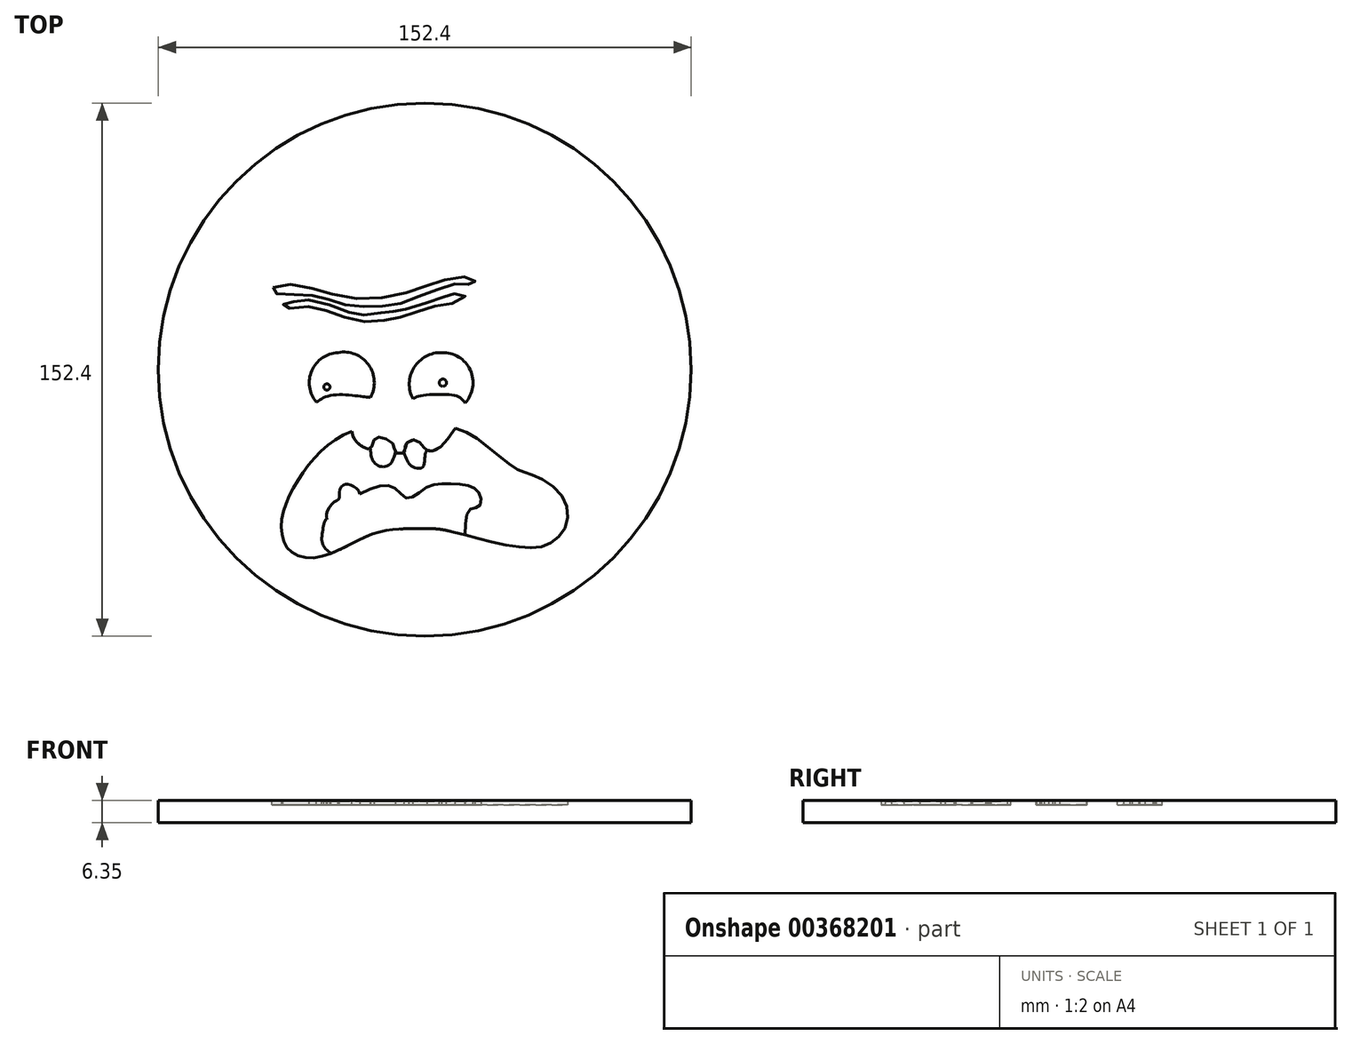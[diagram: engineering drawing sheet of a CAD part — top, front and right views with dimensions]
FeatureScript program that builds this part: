
annotation { "Feature Type Name" : "Feature", "Feature Type Description" : "" }
export const myFeature = defineFeature(function(context is Context, id is Id, definition is map)
    precondition{}
    {
        {
            var Q0;
            Q0=qCreatedBy(makeId("Top.planeOp"),FACE);
            var sketch = newSketch(context, id + "F0", { "sketchPlane" : qUnion([Q0])});
            skLineSegment(sketch, "E0", {"start": v(0, 152.4) * mm, "end": v(153.92, 0) * mm, "construction": true});
            skLineSegment(sketch, "E1", {"start": v(0, 0) * mm, "end": v(153.92, 152.4) * mm, "construction": true});
            skPoint(sketch, "E2", {"position": v(76.96, 76.2) * mm});
            skCircle(sketch, "E3", {"center": v(76.96, 76.2) * mm, "radius": 76.2 * mm});
            skSolve(sketch);
        }
        {
            var Q0;
            Q0 = qSketchRegion(id + "F0", true);
            extrude(context, id + "F1", {"entities" : qUnion([Q0]), "oppositeDirection" : true, "depth" : 6.35 * mm});
        }
        {
            var Q0;
            Q0=makeQuery(id+"F1.opExtrude","CAP_FACE",FACE,{"disambiguationData":[OSD([sQuery(id+"F0.wireOp",EDGE,"E3")])],"isStart":true});
            var sketch = newSketch(context, id + "F2", { "sketchPlane" : qUnion([Q0])});
            skLineSegment(sketch, "E4", {"start": v(0, 152.4) * mm, "end": v(153.92, 0) * mm, "construction": true});
            skLineSegment(sketch, "E5", {"start": v(0, 0) * mm, "end": v(153.92, 152.4) * mm, "construction": true});
            skPoint(sketch, "E6", {"position": v(76.96, 76.2) * mm});
            skArc(sketch, "E7", {"start": v(81.87, 81.06) * mm, "mid": v(73.9, 76.8) * mm, "end": v(73.6, 67.78) * mm});
            skArc(sketch, "E8", {"start": v(88.53, 66.66) * mm, "mid": v(89.97, 76.06) * mm, "end": v(81.87, 81.06) * mm});
            skArc(sketch, "E9", {"start": v(52.16, 81.06) * mm, "mid": v(44.65, 75.9) * mm, "end": v(45.92, 66.89) * mm});
            skCircle(sketch, "E10", {"center": v(48.96, 71.22) * mm, "radius": 0.89 * mm});
            skCircle(sketch, "E11", {"center": v(82.15, 72.45) * mm, "radius": 1.03 * mm});
            skArc(sketch, "E12", {"start": v(61.43, 68.24) * mm, "mid": v(60.86, 77.6) * mm, "end": v(52.16, 81.06) * mm});
            skFitSpline(sketch, "E13", {"points": [v(74.77, 30.7) * mm, v(62.6, 29.38) * mm, v(46.93, 22.64) * mm, v(37.99, 24.84) * mm, v(36.08, 33.34) * mm, v(40.77, 44.62) * mm, v(50.59, 55.6) * mm, v(62.9, 59.71) * mm, v(72.42, 58.4) * mm, v(84.44, 59.57) * mm, v(93.96, 54.88) * mm, v(103.34, 47.7) * mm, v(107.2, 46.27) * mm, v(115.94, 40.52) * mm, v(117.41, 31.87) * mm, v(112.43, 26.3) * mm, v(104.22, 25.42) * mm, v(90.45, 28.35) * mm, v(81.07, 30.55) * mm, v(74.77, 30.7) * mm]});
            skFitSpline(sketch, "E14", {"points": [v(56.15, 58.48) * mm, v(56.85, 56.3) * mm, v(59.27, 54.12) * mm, v(61.43, 53.63) * mm, v(62.6, 56.28) * mm, v(64.81, 56.77) * mm, v(68.2, 54.43) * mm, v(68.57, 52.52) * mm, v(70.98, 52.46) * mm, v(71.47, 54.68) * mm, v(74.36, 56.03) * mm, v(76.64, 54.12) * mm, v(77.57, 53.14) * mm, v(80.83, 53.63) * mm, v(85.2, 58.74) * mm, v(85.7, 59.39) * mm], "startDerivative": vector(6.2, -34.66) * mm, "endDerivative": vector(9.7, 11.43) * mm});
            skFitSpline(sketch, "E15", {"points": [v(50.14, 23.64) * mm, v(47.69, 26.46) * mm, v(48.04, 31.5) * mm, v(49, 33.43) * mm, v(51.09, 31.07) * mm, v(52.05, 31.95) * mm, v(54.22, 32.82) * mm, v(54.4, 36.48) * mm, v(62.24, 42.4) * mm, v(68.34, 42.31) * mm, v(72.09, 39.35) * mm, v(77.23, 42.4) * mm, v(83.15, 43.62) * mm, v(90.04, 42.84) * mm, v(92.74, 40.4) * mm, v(92.48, 37.09) * mm, v(89.86, 36.21) * mm, v(88.46, 28.89) * mm], "startDerivative": vector(-56.66, 43.32) * mm, "endDerivative": vector(-2.65, -124.19) * mm});
            skFitSpline(sketch, "E16", {"points": [v(45.92, 66.89) * mm, v(50.5, 68.88) * mm, v(59.06, 68.5) * mm, v(61.43, 68.24) * mm], "startDerivative": vector(11.59, 7.57) * mm, "endDerivative": vector(8.19, -0.86) * mm});
            skFitSpline(sketch, "E17", {"points": [v(73.6, 67.78) * mm, v(75.08, 68.57) * mm, v(81.92, 69.13) * mm, v(86.72, 68.39) * mm, v(88.53, 66.66) * mm], "startDerivative": vector(6.68, 5.13) * mm, "endDerivative": vector(7.4, -9.56) * mm});
            skFitSpline(sketch, "E18", {"points": [v(33.57, 99.73) * mm, v(40.61, 100.35) * mm, v(49.32, 98.07) * mm, v(61.43, 96.41) * mm, v(73.15, 98.7) * mm, v(80.61, 101.28) * mm, v(88.53, 102.73) * mm, v(91.39, 101.7) * mm, v(90.45, 100.14) * mm, v(88.53, 100.97) * mm, v(83.51, 99.94) * mm, v(76.57, 97.66) * mm, v(69.42, 94.86) * mm, v(62.6, 94.34) * mm, v(55.43, 94.44) * mm, v(49.63, 96.2) * mm, v(43.93, 97.45) * mm, v(37.1, 97.66) * mm, v(33.36, 98.49) * mm, v(33.57, 99.73) * mm]});
            skFitSpline(sketch, "E19", {"points": [v(39.47, 95.6) * mm, v(36.67, 95.08) * mm, v(36.57, 93.84) * mm, v(41.96, 94.15) * mm, v(49.31, 92.9) * mm, v(58.12, 90.1) * mm, v(66.4, 90.42) * mm, v(72, 91.77) * mm, v(79.47, 94.25) * mm, v(86.2, 95.6) * mm, v(88.53, 97.57) * mm, v(84.02, 97.67) * mm, v(82.47, 97.05) * mm, v(73.46, 94.05) * mm, v(68.38, 92.9) * mm, v(66.1, 92.7) * mm, v(59.88, 91.87) * mm, v(55.01, 92.7) * mm, v(44.75, 96.02) * mm, v(39.47, 95.6) * mm]});
            skPoint(sketch, "E20.orphan", {"position": v(50.8, 63.95) * mm});
            skPoint(sketch, "E21.orphan", {"position": v(83.58, 63.95) * mm});
            skSolve(sketch);
        }
        {
            var Q0;
            Q0=makeQuery(id+"F2.imprint","IMPRINT",FACE,{"disambiguationData":[TD([[makeQuery(id+"F2.imprint","IMPRINT",EDGE,{"derivedFrom":sQuery(id+"F2.wireOp",EDGE,"E19")}),1.0]])]});
            var Q1;
            Q1=makeQuery(id+"F2.imprint","IMPRINT",FACE,{"disambiguationData":[TD([[makeQuery(id+"F2.imprint","IMPRINT",EDGE,{"derivedFrom":sQuery(id+"F2.wireOp",EDGE,"E18")}),-1.0]])]});
            var Q2;
            {var subQ0=sQuery(id+"F2.wireOp",EDGE,"E14");Q2=makeQuery(id+"F2.imprint","IMPRINT",FACE,{"disambiguationData":[TD([[makeQuery(id+"F2.imprint","IMPRINT",EDGE,{"derivedFrom":subQ0}),-1.0]])]});}
            var Q3;
            Q3=makeQuery(id+"F2.imprint","IMPRINT",FACE,{"disambiguationData":[TD([[makeQuery(id+"F2.imprint","IMPRINT",EDGE,{"derivedFrom":sQuery(id+"F2.wireOp",EDGE,"E9")}),1.0]])]});
            var Q4;
            Q4=makeQuery(id+"F2.imprint","IMPRINT",FACE,{"disambiguationData":[TD([[makeQuery(id+"F2.imprint","IMPRINT",EDGE,{"derivedFrom":sQuery(id+"F2.wireOp",EDGE,"E7")}),1.0]])]});
            extrude(context, id + "F3", {"entities" : qUnion([Q0, Q1, Q2, Q3, Q4]), "operationType" : NewBodyOperationType.REMOVE, "oppositeDirection" : true, "depth" : 1.27 * mm});
        }
        {
            var Q0;
            {var subQ3=sQuery(id+"F0.wireOp",EDGE,"E3");Q0=makeQuery(id+"F3.boolean.opBoolean","SPLIT",FACE,{"disambiguationData":[TD([makeQuery(id+"F1.opExtrude","SWEPT_FACE",FACE,{"disambiguationData":[OSD([subQ3])]})])],"derivedFrom":makeQuery(id+"F1.opExtrude","CAP_FACE",FACE,{"disambiguationData":[OSD([subQ3])],"isStart":true})});}
            var sketch = newSketch(context, id + "F4", { "sketchPlane" : qUnion([Q0])});
            skLineSegment(sketch, "E22", {"start": v(0, 152.4) * mm, "end": v(153.92, 0) * mm, "construction": true});
            skLineSegment(sketch, "E23", {"start": v(0, 0) * mm, "end": v(153.92, 152.4) * mm, "construction": true});
            skPoint(sketch, "E24", {"position": v(76.96, 76.2) * mm});
            skArc(sketch, "E25", {"start": v(81.87, 81.06) * mm, "mid": v(73.9, 76.8) * mm, "end": v(73.6, 67.78) * mm});
            skArc(sketch, "E26", {"start": v(88.53, 66.66) * mm, "mid": v(89.97, 76.06) * mm, "end": v(81.87, 81.06) * mm});
            skArc(sketch, "E27", {"start": v(52.16, 81.06) * mm, "mid": v(44.65, 75.9) * mm, "end": v(45.92, 66.89) * mm});
            skCircle(sketch, "E28", {"center": v(48.96, 71.22) * mm, "radius": 0.89 * mm});
            skCircle(sketch, "E29", {"center": v(82.15, 72.45) * mm, "radius": 1.03 * mm});
            skArc(sketch, "E30", {"start": v(61.43, 68.24) * mm, "mid": v(60.86, 77.6) * mm, "end": v(52.16, 81.06) * mm});
            skFitSpline(sketch, "E31", {"points": [v(74.77, 30.7) * mm, v(62.6, 29.38) * mm, v(46.93, 22.64) * mm, v(37.99, 24.84) * mm, v(36.08, 33.34) * mm, v(40.77, 44.62) * mm, v(50.59, 55.6) * mm, v(62.9, 59.71) * mm, v(72.42, 58.4) * mm, v(84.44, 59.57) * mm, v(93.96, 54.88) * mm, v(103.34, 47.7) * mm, v(107.2, 46.27) * mm, v(115.94, 40.52) * mm, v(117.41, 31.87) * mm, v(112.43, 26.3) * mm, v(104.22, 25.42) * mm, v(90.45, 28.35) * mm, v(81.07, 30.55) * mm, v(74.77, 30.7) * mm]});
            skFitSpline(sketch, "E32", {"points": [v(56.15, 58.48) * mm, v(56.85, 56.3) * mm, v(59.27, 54.12) * mm, v(61.43, 53.63) * mm, v(62.6, 56.28) * mm, v(64.81, 56.77) * mm, v(68.2, 54.43) * mm, v(68.57, 52.52) * mm, v(70.98, 52.46) * mm, v(71.47, 54.68) * mm, v(74.36, 56.03) * mm, v(76.64, 54.12) * mm, v(77.57, 53.14) * mm, v(80.83, 53.63) * mm, v(85.2, 58.74) * mm, v(85.7, 59.39) * mm], "startDerivative": vector(6.2, -34.66) * mm, "endDerivative": vector(9.7, 11.43) * mm});
            skFitSpline(sketch, "E33", {"points": [v(50.14, 23.64) * mm, v(47.69, 26.46) * mm, v(48.04, 31.5) * mm, v(49, 33.43) * mm, v(51.09, 31.07) * mm, v(52.05, 31.95) * mm, v(54.22, 32.82) * mm, v(54.4, 36.48) * mm, v(62.24, 42.4) * mm, v(68.34, 42.31) * mm, v(72.09, 39.35) * mm, v(77.23, 42.4) * mm, v(83.15, 43.62) * mm, v(90.04, 42.84) * mm, v(92.74, 40.4) * mm, v(92.48, 37.09) * mm, v(89.86, 36.21) * mm, v(88.46, 28.89) * mm], "startDerivative": vector(-56.66, 43.32) * mm, "endDerivative": vector(-2.65, -124.19) * mm});
            skFitSpline(sketch, "E34", {"points": [v(45.92, 66.89) * mm, v(50.5, 68.88) * mm, v(59.06, 68.5) * mm, v(61.43, 68.24) * mm], "startDerivative": vector(11.59, 7.57) * mm, "endDerivative": vector(8.19, -0.86) * mm});
            skFitSpline(sketch, "E35", {"points": [v(73.6, 67.78) * mm, v(75.08, 68.57) * mm, v(81.92, 69.13) * mm, v(86.72, 68.39) * mm, v(88.53, 66.66) * mm], "startDerivative": vector(6.68, 5.13) * mm, "endDerivative": vector(7.4, -9.56) * mm});
            skFitSpline(sketch, "E36", {"points": [v(33.57, 99.73) * mm, v(40.61, 100.35) * mm, v(49.32, 98.07) * mm, v(61.43, 96.41) * mm, v(73.15, 98.7) * mm, v(80.61, 101.28) * mm, v(88.53, 102.73) * mm, v(91.39, 101.7) * mm, v(90.45, 100.14) * mm, v(88.53, 100.97) * mm, v(83.51, 99.94) * mm, v(76.57, 97.66) * mm, v(69.42, 94.86) * mm, v(62.6, 94.34) * mm, v(55.43, 94.44) * mm, v(49.63, 96.2) * mm, v(43.93, 97.45) * mm, v(37.1, 97.66) * mm, v(33.36, 98.49) * mm, v(33.57, 99.73) * mm]});
            skFitSpline(sketch, "E37", {"points": [v(39.47, 95.6) * mm, v(36.67, 95.08) * mm, v(36.57, 93.84) * mm, v(41.96, 94.15) * mm, v(49.31, 92.9) * mm, v(58.12, 90.1) * mm, v(66.4, 90.42) * mm, v(72, 91.77) * mm, v(79.47, 94.25) * mm, v(86.2, 95.6) * mm, v(88.53, 97.57) * mm, v(84.02, 97.67) * mm, v(82.47, 97.05) * mm, v(73.46, 94.05) * mm, v(68.38, 92.9) * mm, v(66.1, 92.7) * mm, v(59.88, 91.87) * mm, v(55.01, 92.7) * mm, v(44.75, 96.02) * mm, v(39.47, 95.6) * mm]});
            skPoint(sketch, "E38.orphan", {"position": v(50.8, 63.95) * mm});
            skPoint(sketch, "E39.orphan", {"position": v(83.58, 63.95) * mm});
            skSolve(sketch);
        }
        {
            var Q0;
            Q0=makeQuery(id+"F4.imprint","IMPRINT",FACE,{"disambiguationData":[TD([[makeQuery(id+"F4.imprint","IMPRINT",EDGE,{"derivedFrom":sQuery(id+"F4.wireOp",EDGE,"E33")}),-1.0]])]});
            var Q1;
            Q1=makeQuery(id+"F4.imprint","IMPRINT",FACE,{"disambiguationData":[TD([[makeQuery(id+"F4.imprint","IMPRINT",EDGE,{"derivedFrom":sQuery(id+"F4.wireOp",EDGE,"E31")}),-1.0]])]});
            extrude(context, id + "F5", {"entities" : qUnion([Q0, Q1]), "operationType" : NewBodyOperationType.REMOVE, "oppositeDirection" : true, "depth" : 0.64 * mm});
        }
        {
            var Q0;
            Q0=makeQuery(id+"F3.boolean.opBoolean","COPY",FACE,{"derivedFrom":makeQuery(id+"F3.opExtrude","CAP_FACE",FACE,{"disambiguationData":[OSD([sQuery(id+"F2.wireOp",EDGE,"E13"),sQuery(id+"F2.wireOp",EDGE,"E14"),sQuery(id+"F2.wireOp",EDGE,"E15")])],"isStart":false})});
            var sketch = newSketch(context, id + "F6", { "sketchPlane" : qUnion([Q0])});
            skLineSegment(sketch, "E40", {"start": v(0, 152.4) * mm, "end": v(153.92, 0) * mm, "construction": true});
            skLineSegment(sketch, "E41", {"start": v(0, 0) * mm, "end": v(153.92, 152.4) * mm, "construction": true});
            skPoint(sketch, "E42", {"position": v(76.96, 76.2) * mm});
            skArc(sketch, "E43", {"start": v(81.87, 81.06) * mm, "mid": v(73.9, 76.8) * mm, "end": v(73.6, 67.78) * mm});
            skArc(sketch, "E44", {"start": v(88.53, 66.66) * mm, "mid": v(89.97, 76.06) * mm, "end": v(81.87, 81.06) * mm});
            skArc(sketch, "E45", {"start": v(52.16, 81.06) * mm, "mid": v(44.65, 75.9) * mm, "end": v(45.92, 66.89) * mm});
            skCircle(sketch, "E46", {"center": v(48.96, 71.22) * mm, "radius": 0.89 * mm});
            skCircle(sketch, "E47", {"center": v(82.15, 72.45) * mm, "radius": 1.03 * mm});
            skArc(sketch, "E48", {"start": v(61.43, 68.24) * mm, "mid": v(60.86, 77.6) * mm, "end": v(52.16, 81.06) * mm});
            skFitSpline(sketch, "E49", {"points": [v(74.77, 30.7) * mm, v(62.6, 29.38) * mm, v(46.93, 22.64) * mm, v(37.99, 24.84) * mm, v(36.08, 33.34) * mm, v(40.77, 44.62) * mm, v(50.59, 55.6) * mm, v(62.9, 59.71) * mm, v(72.42, 58.4) * mm, v(84.44, 59.57) * mm, v(93.96, 54.88) * mm, v(103.34, 47.7) * mm, v(107.2, 46.27) * mm, v(115.94, 40.52) * mm, v(117.41, 31.87) * mm, v(112.43, 26.3) * mm, v(104.22, 25.42) * mm, v(90.45, 28.35) * mm, v(81.07, 30.55) * mm, v(74.77, 30.7) * mm]});
            skFitSpline(sketch, "E50", {"points": [v(56.15, 58.48) * mm, v(56.85, 56.3) * mm, v(59.27, 54.12) * mm, v(61.43, 53.63) * mm, v(62.6, 56.28) * mm, v(64.81, 56.77) * mm, v(68.2, 54.43) * mm, v(68.57, 52.52) * mm, v(70.98, 52.46) * mm, v(71.47, 54.68) * mm, v(74.36, 56.03) * mm, v(76.64, 54.12) * mm, v(77.57, 53.14) * mm, v(80.83, 53.63) * mm, v(85.2, 58.74) * mm, v(85.7, 59.39) * mm], "startDerivative": vector(6.2, -34.66) * mm, "endDerivative": vector(9.7, 11.43) * mm});
            skFitSpline(sketch, "E51", {"points": [v(50.14, 23.64) * mm, v(47.69, 26.46) * mm, v(48.04, 31.5) * mm, v(49, 33.43) * mm, v(51.09, 31.07) * mm, v(52.05, 31.95) * mm, v(54.22, 32.82) * mm, v(54.4, 36.48) * mm, v(62.24, 42.4) * mm, v(68.34, 42.31) * mm, v(72.09, 39.35) * mm, v(77.23, 42.4) * mm, v(83.15, 43.62) * mm, v(90.04, 42.84) * mm, v(92.74, 40.4) * mm, v(92.48, 37.09) * mm, v(89.86, 36.21) * mm, v(88.46, 28.89) * mm], "startDerivative": vector(-56.66, 43.32) * mm, "endDerivative": vector(-2.65, -124.19) * mm});
            skFitSpline(sketch, "E52", {"points": [v(45.92, 66.89) * mm, v(50.5, 68.88) * mm, v(59.06, 68.5) * mm, v(61.43, 68.24) * mm], "startDerivative": vector(11.59, 7.57) * mm, "endDerivative": vector(8.19, -0.86) * mm});
            skFitSpline(sketch, "E53", {"points": [v(73.6, 67.78) * mm, v(75.08, 68.57) * mm, v(81.92, 69.13) * mm, v(86.72, 68.39) * mm, v(88.53, 66.66) * mm], "startDerivative": vector(6.68, 5.13) * mm, "endDerivative": vector(7.4, -9.56) * mm});
            skFitSpline(sketch, "E54", {"points": [v(33.57, 99.73) * mm, v(40.61, 100.35) * mm, v(49.32, 98.07) * mm, v(61.43, 96.41) * mm, v(73.15, 98.7) * mm, v(80.61, 101.28) * mm, v(88.53, 102.73) * mm, v(91.39, 101.7) * mm, v(90.45, 100.14) * mm, v(88.53, 100.97) * mm, v(83.51, 99.94) * mm, v(76.57, 97.66) * mm, v(69.42, 94.86) * mm, v(62.6, 94.34) * mm, v(55.43, 94.44) * mm, v(49.63, 96.2) * mm, v(43.93, 97.45) * mm, v(37.1, 97.66) * mm, v(33.36, 98.49) * mm, v(33.57, 99.73) * mm]});
            skFitSpline(sketch, "E55", {"points": [v(39.47, 95.6) * mm, v(36.67, 95.08) * mm, v(36.57, 93.84) * mm, v(41.96, 94.15) * mm, v(49.31, 92.9) * mm, v(58.12, 90.1) * mm, v(66.4, 90.42) * mm, v(72, 91.77) * mm, v(79.47, 94.25) * mm, v(86.2, 95.6) * mm, v(88.53, 97.57) * mm, v(84.02, 97.67) * mm, v(82.47, 97.05) * mm, v(73.46, 94.05) * mm, v(68.38, 92.9) * mm, v(66.1, 92.7) * mm, v(59.88, 91.87) * mm, v(55.01, 92.7) * mm, v(44.75, 96.02) * mm, v(39.47, 95.6) * mm]});
            skPoint(sketch, "E56.orphan", {"position": v(50.8, 63.95) * mm});
            skPoint(sketch, "E57.orphan", {"position": v(83.58, 63.95) * mm});
            skFitSpline(sketch, "E58", {"points": [v(61.43, 53.63) * mm, v(62.14, 50.12) * mm, v(64.33, 48.5) * mm, v(66.9, 49.02) * mm, v(68.57, 52.52) * mm], "startDerivative": vector(0.96, -14.5) * mm, "endDerivative": vector(4.5, 15.13) * mm});
            skFitSpline(sketch, "E59", {"points": [v(70.98, 52.46) * mm, v(72.32, 49.53) * mm, v(73.64, 48.28) * mm, v(76.35, 48.28) * mm, v(77, 51.58) * mm, v(77.57, 53.14) * mm], "startDerivative": vector(5.96, -14.35) * mm, "endDerivative": vector(4.3, 7.74) * mm});
            skFitSpline(sketch, "E60", {"points": [v(49, 33.43) * mm, v(49, 35.6) * mm, v(51.37, 38.54) * mm, v(52.54, 39.42) * mm, v(52.54, 41.47) * mm, v(53.78, 43.23) * mm, v(55.62, 43.23) * mm, v(57.81, 41.9) * mm, v(58.18, 41.18) * mm, v(58.38, 40.58) * mm], "startDerivative": vector(-3.5, 17) * mm, "endDerivative": vector(3.16, -9.2) * mm});
            skFitSpline(sketch, "E61", {"points": [v(90.04, 42.84) * mm, v(91.15, 44.18) * mm, v(93.42, 44.4) * mm, v(95.55, 42.84) * mm, v(96.8, 40.96) * mm, v(98.48, 38.47) * mm, v(97.96, 34.07) * mm, v(96.94, 32.24) * mm, v(95.47, 31.8) * mm, v(94.89, 28.87) * mm, v(94.66, 27.27) * mm], "startDerivative": vector(10.47, 18.09) * mm, "endDerivative": vector(-3.33, -16.22) * mm});
            skFitSpline(sketch, "E62", {"points": [v(55.67, 26.27) * mm, v(54, 29.3) * mm, v(56.07, 32) * mm, v(59.49, 32) * mm, v(60.1, 29.4) * mm, v(60.35, 28.53) * mm], "startDerivative": vector(-11.1, 13.13) * mm, "endDerivative": vector(2.58, -6) * mm});
            skFitSpline(sketch, "E63", {"points": [v(64.49, 29.9) * mm, v(64.56, 31.59) * mm, v(68.3, 32.62) * mm, v(70.58, 30.66) * mm], "startDerivative": vector(-1.9, 6.9) * mm, "endDerivative": vector(5.15, -7.52) * mm});
            skFitSpline(sketch, "E64", {"points": [v(78.55, 30.72) * mm, v(81.07, 33.35) * mm, v(84.35, 32.1) * mm, v(85.6, 29.64) * mm], "startDerivative": vector(6.15, 10.15) * mm, "endDerivative": vector(2.56, -8.49) * mm});
            skLineSegment(sketch, "E65", {"start": v(55.67, 26.27) * mm, "end": v(60.35, 28.53) * mm});
            skLineSegment(sketch, "E66", {"start": v(64.49, 29.9) * mm, "end": v(70.58, 30.66) * mm});
            skLineSegment(sketch, "E67", {"start": v(78.55, 30.72) * mm, "end": v(85.6, 29.64) * mm});
            skSolve(sketch);
        }
        {
            var Q0;
            Q0=makeQuery(id+"F6.imprint","IMPRINT",FACE,{"disambiguationData":[TD([[makeQuery(id+"F6.imprint","IMPRINT",EDGE,{"derivedFrom":sQuery(id+"F6.wireOp",EDGE,"E51")}),1.0]])]});
            var Q1;
            Q1=makeQuery(id+"F6.imprint","IMPRINT",FACE,{"disambiguationData":[TD([[makeQuery(id+"F6.imprint","IMPRINT",EDGE,{"derivedFrom":sQuery(id+"F6.wireOp",EDGE,"E49")}),-1.0]])]});
            var Q2;
            {var subQ0=sQuery(id+"F6.wireOp",EDGE,"E59");Q2=makeQuery(id+"F6.imprint","IMPRINT",FACE,{"disambiguationData":[TD([[makeQuery(id+"F6.imprint","IMPRINT",EDGE,{"derivedFrom":subQ0}),1.0]])]});}
            var Q3;
            {var subQ0=sQuery(id+"F6.wireOp",EDGE,"E58");Q3=makeQuery(id+"F6.imprint","IMPRINT",FACE,{"disambiguationData":[TD([[makeQuery(id+"F6.imprint","IMPRINT",EDGE,{"derivedFrom":subQ0}),1.0]])]});}
            var Q4;
            {var subQ0=sQuery(id+"F6.wireOp",EDGE,"E62");Q4=makeQuery(id+"F6.imprint","IMPRINT",FACE,{"disambiguationData":[TD([[makeQuery(id+"F6.imprint","IMPRINT",EDGE,{"derivedFrom":subQ0}),-1.0]])]});}
            var Q5;
            {var subQ0=sQuery(id+"F6.wireOp",EDGE,"E63");Q5=makeQuery(id+"F6.imprint","IMPRINT",FACE,{"disambiguationData":[TD([[makeQuery(id+"F6.imprint","IMPRINT",EDGE,{"derivedFrom":subQ0}),-1.0]])]});}
            var Q6;
            {var subQ0=sQuery(id+"F6.wireOp",EDGE,"E64");Q6=makeQuery(id+"F6.imprint","IMPRINT",FACE,{"disambiguationData":[TD([[makeQuery(id+"F6.imprint","IMPRINT",EDGE,{"derivedFrom":subQ0}),-1.0]])]});}
            extrude(context, id + "F7", {"entities" : qUnion([Q0, Q1, Q2, Q3, Q4, Q5, Q6]), "operationType" : NewBodyOperationType.ADD, "depth" : 1.02 * mm});
        }
    });
